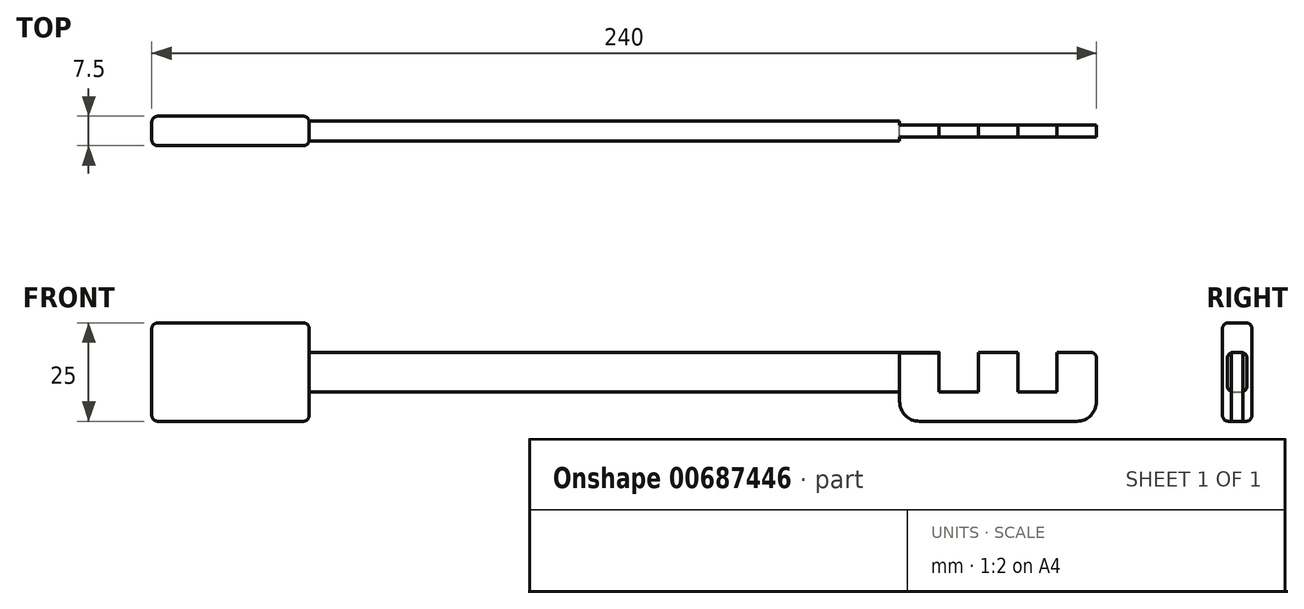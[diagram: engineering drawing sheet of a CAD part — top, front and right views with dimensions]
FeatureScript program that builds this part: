
annotation { "Feature Type Name" : "Feature", "Feature Type Description" : "" }
export const myFeature = defineFeature(function(context is Context, id is Id, definition is map)
    precondition{}
    {
        {
            var Q0;
            Q0=qCreatedBy(makeId("Front.planeOp"),FACE);
            var sketch = newSketch(context, id + "F0", { "sketchPlane" : qUnion([Q0])});
            skLineSegment(sketch, "E0.bottom", {"start": v(281.54, -12.5) * mm, "end": v(241.54, -12.5) * mm});
            skLineSegment(sketch, "E0.top", {"start": v(281.54, 12.5) * mm, "end": v(241.54, 12.5) * mm});
            skLineSegment(sketch, "E0.left", {"start": v(281.54, -12.5) * mm, "end": v(281.54, 12.5) * mm});
            skLineSegment(sketch, "E0.right", {"start": v(241.54, -12.5) * mm, "end": v(241.54, 12.5) * mm});
            skPoint(sketch, "E0.middle", {"position": v(261.54, 0) * mm});
            skLineSegment(sketch, "E1.bottom", {"start": v(281.54, 0) * mm, "end": v(431.54, 0) * mm});
            skLineSegment(sketch, "E1.top", {"start": v(281.54, 5) * mm, "end": v(431.54, 5) * mm});
            skLineSegment(sketch, "E1.left", {"start": v(281.54, 0) * mm, "end": v(281.54, 5) * mm});
            skLineSegment(sketch, "E1.right", {"start": v(431.54, 0) * mm, "end": v(431.54, 5) * mm});
            skLineSegment(sketch, "E2.MirrorCS", {"start": v(281.54, -5) * mm, "end": v(431.54, -5) * mm});
            skLineSegment(sketch, "E3.MirrorCS", {"start": v(431.54, 0) * mm, "end": v(431.54, -5) * mm});
            skLineSegment(sketch, "E4.bottom", {"start": v(431.54, 5) * mm, "end": v(481.54, 5) * mm});
            skLineSegment(sketch, "E4.top", {"start": v(431.54, -12.5) * mm, "end": v(481.54, -12.5) * mm});
            skLineSegment(sketch, "E4.left", {"start": v(431.54, 5) * mm, "end": v(431.54, -12.5) * mm});
            skLineSegment(sketch, "E4.right", {"start": v(481.54, 5) * mm, "end": v(481.54, -12.5) * mm});
            skLineSegment(sketch, "E5.bottom", {"start": v(441.54, 5) * mm, "end": v(451.54, 5) * mm});
            skLineSegment(sketch, "E5.top", {"start": v(441.54, -5) * mm, "end": v(451.54, -5) * mm});
            skLineSegment(sketch, "E5.left", {"start": v(441.54, 5) * mm, "end": v(441.54, -5) * mm});
            skLineSegment(sketch, "E5.right", {"start": v(451.54, 5) * mm, "end": v(451.54, -5) * mm});
            skLineSegment(sketch, "E6.bottom", {"start": v(461.54, 5) * mm, "end": v(471.54, 5) * mm});
            skLineSegment(sketch, "E6.top", {"start": v(461.54, -5) * mm, "end": v(471.54, -5) * mm});
            skLineSegment(sketch, "E6.left", {"start": v(461.54, 5) * mm, "end": v(461.54, -5) * mm});
            skLineSegment(sketch, "E6.right", {"start": v(471.54, 5) * mm, "end": v(471.54, -5) * mm});
            skSolve(sketch);
        }
        {
            var Q0;
            {var subQ4=sQuery(id+"F0.wireOp",EDGE,"E4.top");Q0=makeQuery(id+"F0.imprint","IMPRINT",FACE,{"disambiguationData":[TD([[makeQuery(id+"F0.imprint","IMPRINT",EDGE,{"derivedFrom":subQ4}),1.0]])]});}
            extrude(context, id + "F1", {"entities" : qUnion([Q0]), "endBound" : BoundingType.SYMMETRIC, "depth" : 3 * mm, "offsetDistance" : 25 * mm});
        }
        {
            var Q0;
            {var subQ0=sQuery(id+"F0.wireOp",EDGE,"E1.bottom");Q0=makeQuery(id+"F0.imprint","IMPRINT",FACE,{"disambiguationData":[TD([[makeQuery(id+"F0.imprint","IMPRINT",EDGE,{"derivedFrom":subQ0}),-1.0]])]});}
            var Q1;
            {var subQ0=sQuery(id+"F0.wireOp",EDGE,"E1.bottom");Q1=makeQuery(id+"F0.imprint","IMPRINT",FACE,{"disambiguationData":[TD([[makeQuery(id+"F0.imprint","IMPRINT",EDGE,{"derivedFrom":subQ0}),1.0]])]});}
            extrude(context, id + "F2", {"entities" : qUnion([Q0, Q1]), "operationType" : NewBodyOperationType.ADD, "endBound" : BoundingType.SYMMETRIC, "depth" : 5 * mm, "offsetDistance" : 25 * mm});
        }
        {
            var Q0;
            {var subQ3=sQuery(id+"F0.wireOp",EDGE,"E0.bottom");Q0=makeQuery(id+"F0.imprint","IMPRINT",FACE,{"disambiguationData":[TD([[makeQuery(id+"F0.imprint","IMPRINT",EDGE,{"derivedFrom":subQ3}),-1.0]])]});}
            extrude(context, id + "F3", {"entities" : qUnion([Q0]), "operationType" : NewBodyOperationType.ADD, "endBound" : BoundingType.SYMMETRIC, "depth" : 7.5 * mm, "offsetDistance" : 25 * mm});
        }
        {
            var Q0;
            Q0=makeQuery(id+"F3.opExtrude","CAP_FACE",FACE,{"disambiguationData":[OSD([sQuery(id+"F0.wireOp",EDGE,"E0.bottom"),sQuery(id+"F0.wireOp",EDGE,"E0.top"),sQuery(id+"F0.wireOp",EDGE,"E0.left"),sQuery(id+"F0.wireOp",EDGE,"E0.right"),sQuery(id+"F0.wireOp",EDGE,"E1.left")])],"isStart":false});
            var Q1;
            Q1=makeQuery(id+"F3.opExtrude","CAP_FACE",FACE,{"disambiguationData":[OSD([sQuery(id+"F0.wireOp",EDGE,"E0.bottom"),sQuery(id+"F0.wireOp",EDGE,"E0.top"),sQuery(id+"F0.wireOp",EDGE,"E0.left"),sQuery(id+"F0.wireOp",EDGE,"E0.right"),sQuery(id+"F0.wireOp",EDGE,"E1.left")])],"isStart":true});
            var Q2;
            Q2=makeQuery(id+"F3.opExtrude","SWEPT_FACE",FACE,{"disambiguationData":[OSD([sQuery(id+"F0.wireOp",EDGE,"E0.right")])]});
            var Q3;
            Q3=makeQuery(id+"F3.opExtrude","SWEPT_EDGE",EDGE,{"disambiguationData":[OSD([sQuery(id+"F0.wireOp",EDGE,"E0.top"),sQuery(id+"F0.wireOp",EDGE,"E0.left")])]});
            var Q4;
            Q4=makeQuery(id+"F3.opExtrude","SWEPT_EDGE",EDGE,{"disambiguationData":[OSD([sQuery(id+"F0.wireOp",EDGE,"E0.bottom"),sQuery(id+"F0.wireOp",EDGE,"E0.left")])]});
            fillet(context, id + "F4", {"entities" : qUnion([Q0, Q1, Q2, Q3, Q4]), "radius" : 1.5 * mm, "tangentPropagation" : true, "allowEdgeOverflow" : false});
        }
        {
            var Q0;
            Q0=makeQuery(id+"F2.opExtrude","CAP_EDGE",EDGE,{"disambiguationData":[OSD([sQuery(id+"F0.wireOp",EDGE,"E1.top")])],"isStart":false});
            var Q1;
            Q1=makeQuery(id+"F2.opExtrude","CAP_EDGE",EDGE,{"disambiguationData":[OSD([sQuery(id+"F0.wireOp",EDGE,"E2.MirrorCS")])],"isStart":false});
            var Q2;
            Q2=makeQuery(id+"F2.opExtrude","CAP_EDGE",EDGE,{"disambiguationData":[OSD([sQuery(id+"F0.wireOp",EDGE,"E1.top")])],"isStart":true});
            var Q3;
            Q3=makeQuery(id+"F2.opExtrude","CAP_EDGE",EDGE,{"disambiguationData":[OSD([sQuery(id+"F0.wireOp",EDGE,"E2.MirrorCS")])],"isStart":true});
            var Q4;
            Q4=makeQuery(id+"F1.opExtrude","SWEPT_EDGE",EDGE,{"disambiguationData":[OSD([sQuery(id+"F0.wireOp",EDGE,"E4.bottom"),sQuery(id+"F0.wireOp",EDGE,"E4.right")])]});
            fillet(context, id + "F5", {"entities" : qUnion([Q0, Q1, Q2, Q3, Q4]), "radius" : 1.5 * mm, "tangentPropagation" : true, "allowEdgeOverflow" : false});
        }
        {
            var Q0;
            Q0=makeQuery(id+"F1.opExtrude","SWEPT_EDGE",EDGE,{"disambiguationData":[OSD([sQuery(id+"F0.wireOp",EDGE,"E4.top"),sQuery(id+"F0.wireOp",EDGE,"E4.right")])]});
            var Q1;
            Q1=makeQuery(id+"F1.opExtrude","SWEPT_EDGE",EDGE,{"disambiguationData":[OSD([sQuery(id+"F0.wireOp",EDGE,"E4.top"),sQuery(id+"F0.wireOp",EDGE,"E4.left")])]});
            fillet(context, id + "F6", {"entities" : qUnion([Q0, Q1]), "radius" : 5 * mm, "tangentPropagation" : true, "allowEdgeOverflow" : false});
        }
    });
